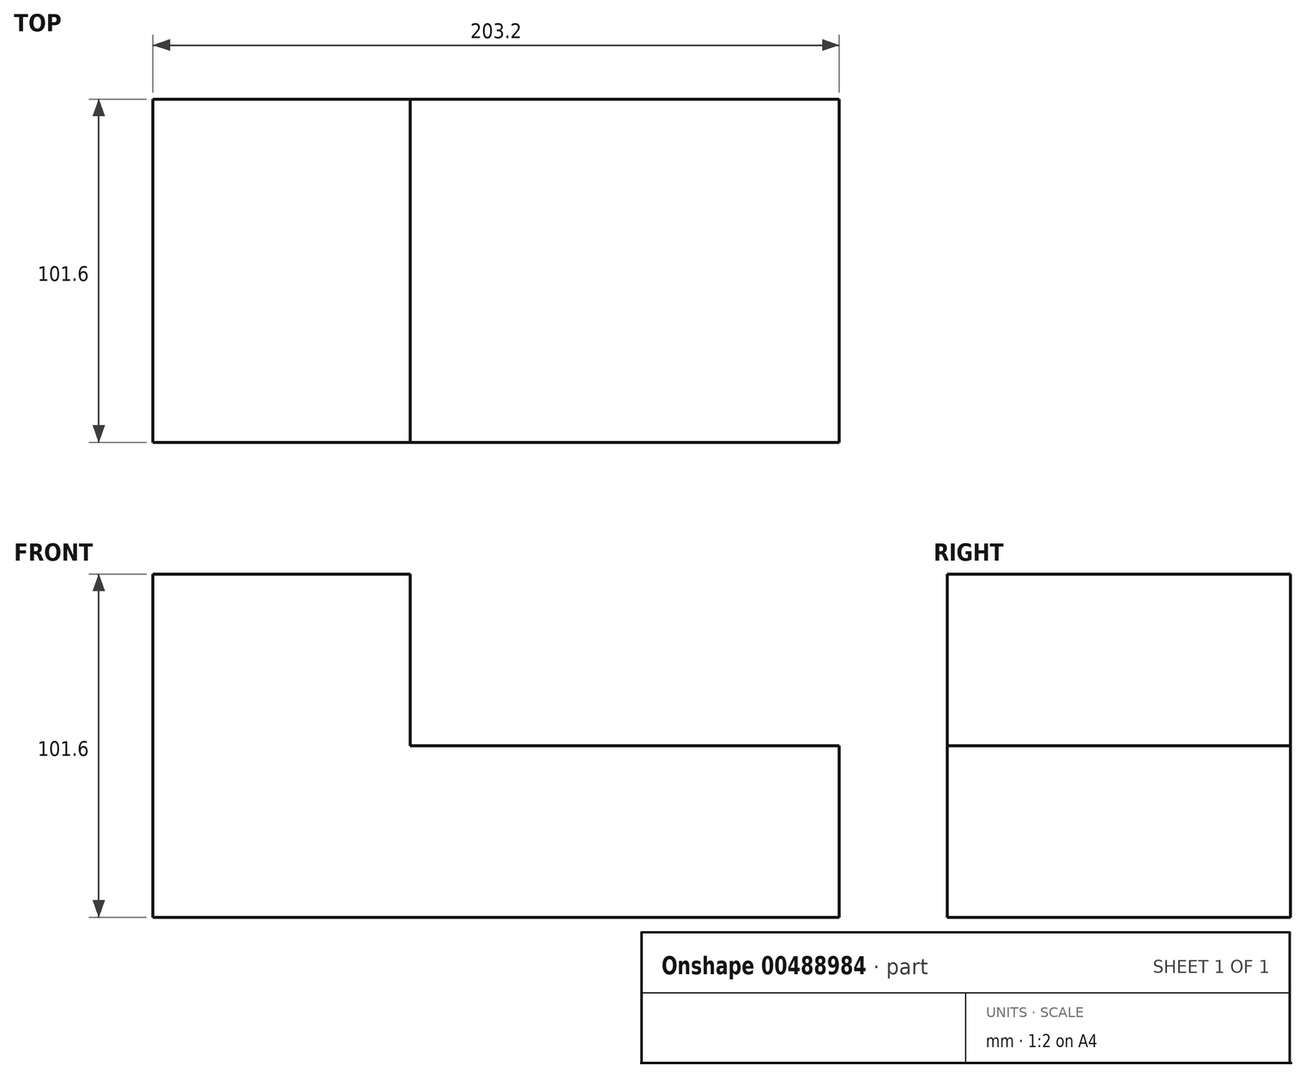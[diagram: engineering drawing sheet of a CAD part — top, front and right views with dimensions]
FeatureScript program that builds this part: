
annotation { "Feature Type Name" : "Feature", "Feature Type Description" : "" }
export const myFeature = defineFeature(function(context is Context, id is Id, definition is map)
    precondition{}
    {
        {
            var Q0;
            Q0=qCreatedBy(makeId("Front.planeOp"),FACE);
            var sketch = newSketch(context, id + "F0", { "sketchPlane" : qUnion([Q0])});
            skLineSegment(sketch, "E0.bottom", {"start": v(-63.82, 23.12) * mm, "end": v(139.38, 23.12) * mm});
            skLineSegment(sketch, "E0.top", {"start": v(-63.82, -27.68) * mm, "end": v(139.38, -27.68) * mm});
            skLineSegment(sketch, "E0.left", {"start": v(-63.82, 23.12) * mm, "end": v(-63.82, -27.68) * mm});
            skLineSegment(sketch, "E0.right", {"start": v(139.38, 23.12) * mm, "end": v(139.38, -27.68) * mm});
            skLineSegment(sketch, "E1.bottom", {"start": v(-63.82, 23.12) * mm, "end": v(12.38, 23.12) * mm});
            skLineSegment(sketch, "E1.top", {"start": v(-63.82, 73.92) * mm, "end": v(12.38, 73.92) * mm});
            skLineSegment(sketch, "E1.left", {"start": v(-63.82, 23.12) * mm, "end": v(-63.82, 73.92) * mm});
            skLineSegment(sketch, "E1.right", {"start": v(12.38, 23.12) * mm, "end": v(12.38, 73.92) * mm});
            skSolve(sketch);
        }
        {
            var Q0;
            Q0 = qSketchRegion(id + "F0", true);
            extrude(context, id + "F1", {"entities" : qUnion([Q0]), "depth" : 101.6 * mm});
        }
    });
